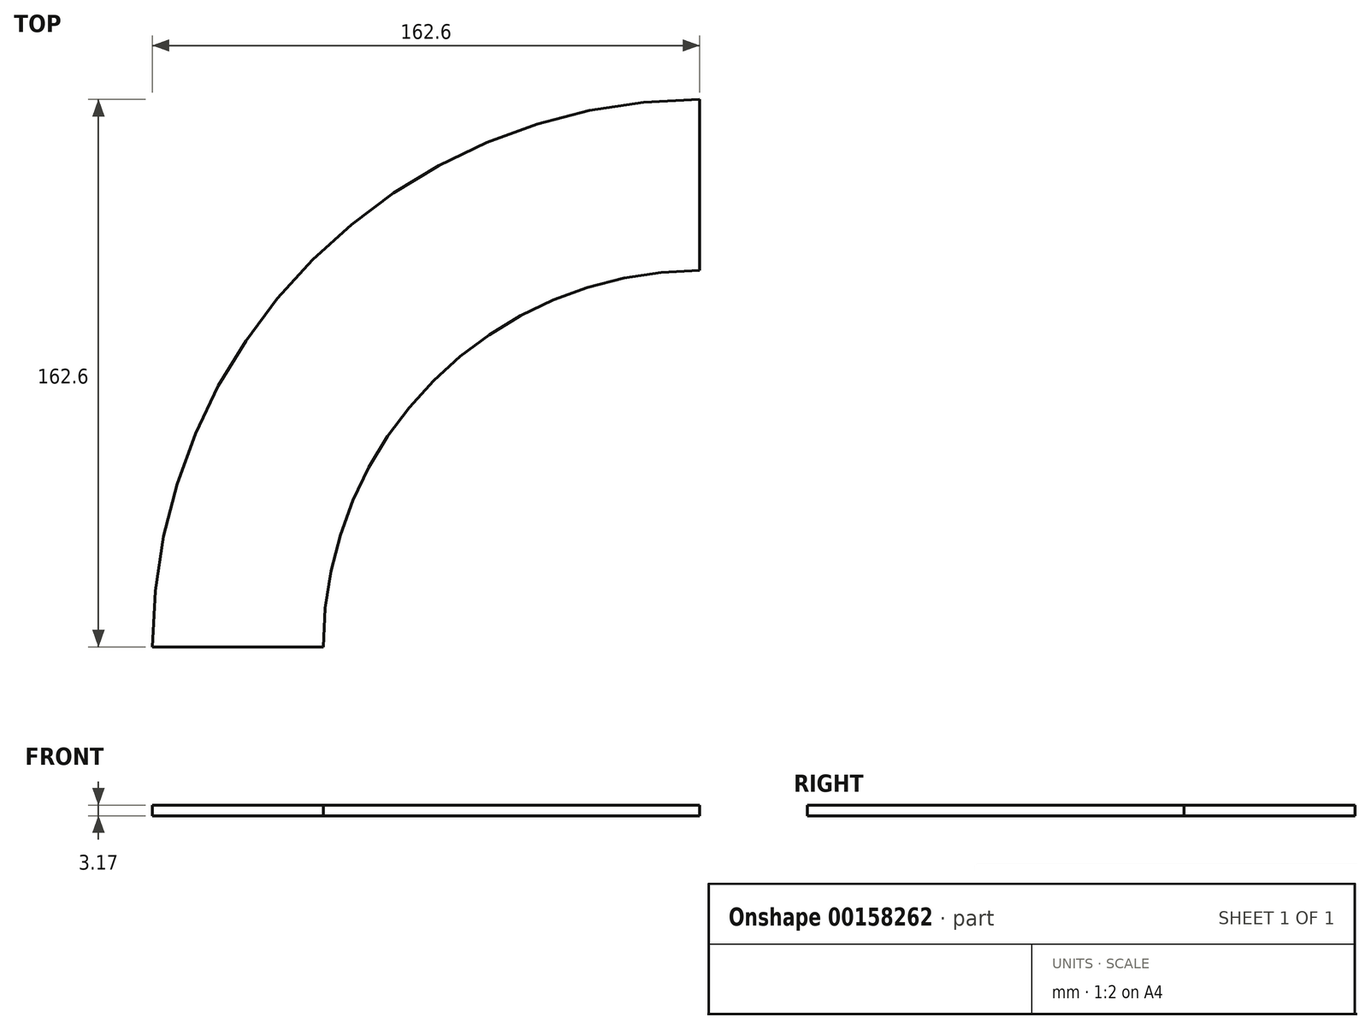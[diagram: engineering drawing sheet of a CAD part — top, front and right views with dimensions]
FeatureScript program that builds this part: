
annotation { "Feature Type Name" : "Feature", "Feature Type Description" : "" }
export const myFeature = defineFeature(function(context is Context, id is Id, definition is map)
    precondition{}
    {
        {
            var Q0;
            Q0=qCreatedBy(makeId("Top.planeOp"),FACE);
            var sketch = newSketch(context, id + "F0", { "sketchPlane" : qUnion([Q0])});
            skCircle(sketch, "E0", {"center": v(0, 0) * mm, "radius": 162.6 * mm});
            skCircle(sketch, "E1", {"center": v(0, 0) * mm, "radius": 111.8 * mm});
            skLineSegment(sketch, "E2", {"start": v(0, 212.91) * mm, "end": v(0, -259.24) * mm});
            skLineSegment(sketch, "E3", {"start": v(-279.86, 0) * mm, "end": v(300.14, 0) * mm});
            skSolve(sketch);
        }
        {
            var Q0;
            {var subQ0=sQuery(id+"F0.wireOp",EDGE,"E2");var subQ1=sQuery(id+"F0.wireOp",EDGE,"E0");var subQ2=makeQuery(id+"F0.imprint","INTERSECT",VERTEX,{"disambiguationData":[OD(0.0)],"derivedFrom":[subQ1,subQ0]});Q0=makeQuery(id+"F0.imprint","IMPRINT",FACE,{"disambiguationData":[TD([[makeQuery(id+"F0.imprint","IMPRINT",EDGE,{"disambiguationData":[TD([[subQ2,-1.0]])],"derivedFrom":subQ1}),1.0]])]});}
            extrude(context, id + "F1", {"entities" : qUnion([Q0]), "depth" : 3.17 * mm});
        }
    });
